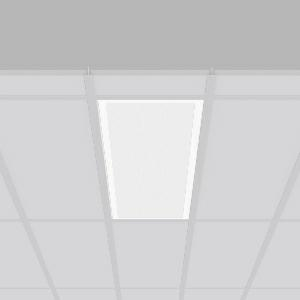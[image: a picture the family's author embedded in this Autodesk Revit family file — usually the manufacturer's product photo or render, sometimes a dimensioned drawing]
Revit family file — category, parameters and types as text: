
# Revit family: sidelite_eco_672373_002_4419
name_source: partatom
category: Lighting Fixtures
units: mm (PartAtom-declared; Revit-internal decimal feet)

## family parameters
Cut with Voids When Loaded = No
Host = Face
Light Source = No
Part Type = Normal
Room Calculation Point = No
Round Connector Dimension = Use Diameter
Shared = No

## types (1)
- SIDELITE ECO (1 x LED Modul 830, 3150 lm, 3000)
    Apparent Load = 29 VA
    CIE Flux Codes = 60 87 97 100 100
    Color Rendering = 80
    Color Temperature = 3000
    Default Elevation = 1800 mm
    Description = Series: SIDELITE ECO
Highly economical recessed luminaire with progressive LED technology. For escape route illumination. Frame made of aluminium, powder-coated. Diffuser plastic microprismatic. Lightguide and diffuser made of non-yellowing plastic (PMMA). Lateral light emission (RZB SIDELITE technology) for homogeneous light distribution. External driver. Second cable inlet for loop through. External driver with simple plug-in locking system. Extended connection cable (1.90 m). Suitable for connection to central battery systems. 
Colour: white
Length: 1245 mm
Width: 308 mm
Cut-out length: 1220 mm
Cut-out width: 285 mm
Recess height: 160 mm
Luminaire: recess height: 40 mm
Weight: 3.64 kg
Operating mode: maintained power mode
Lamp: LED
Socket: without socket
Colour temperature: 3000K
Colour rendering index (CRI): 80
System power: 29 W
Rated luminous flux: 3150 lm
Luminous flux, emergency: 3150 lm
System power, emergency: 29 W
Control gear: Regulated power supply
Protection class: II
Type of protection: IP 20
    Height = 0 mm  [stored 0 ft]
    Lamp = 1 x LED Modul 830
    Lamp Light Flux = 3150 lm
    Lamp count = 1
    Length = 1245 mm
    Lifetime = 50000 h
    Luminous efficacy = 109 lm/W
    Manufacturer = RZB
    ModVariant = No
    Model = 672373.002
    Mounting Place = Ceiling
    Mounting Type = Recessed
    Number of Poles = 1
    OnlyDefault = Yes
    Power Factor = 1
    Product Name = SIDELITE ECO
    Product group = Recessed modular luminaires
    ProductGroupID = 406
    Protection Class = Protection class II
    Protection Degree = IP 20
    RLX_Detail_Level = 1
    RLX_Emergency_Light_Flux = 3150 lm
    RLX_Emergency_Type = 3
    RLX_Emergency_Type_DB = Yes
    RlxData = <blob elided: 34165 chars, md5=24c3833f>
    Socket = socket
    Standby Power = 0 W
    System Light Flux = 3150 lm
    System Power = 29 W
    Type Comments = Product without accessories
    Type Image = 312368.002.jpg
    URL = http://relux.com
    VarID = ---
    Voltage = 230 V
    Voltage Range = 220-240 V
    Weight = 0.00 kg
    Width = 308 mm

note: [stored X ft] marks values corroborated as IEEE doubles in the binary element streams (Revit-internal decimal feet)

## geometry (parser evidence)
native form markers: Blend x4, Sweep x10
no freeform markers — native parametric forms only
